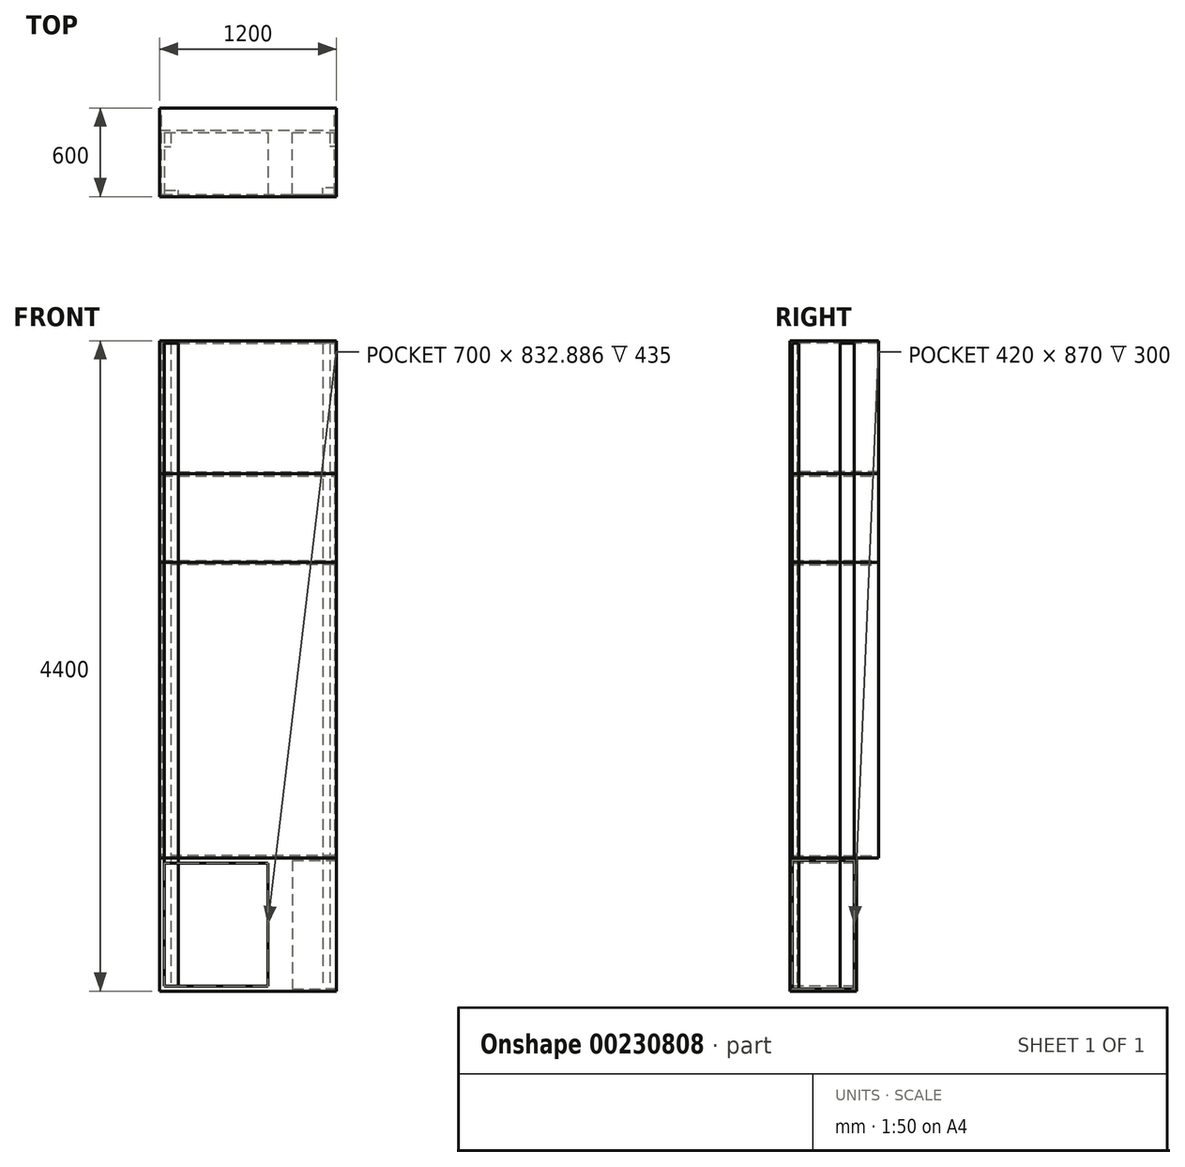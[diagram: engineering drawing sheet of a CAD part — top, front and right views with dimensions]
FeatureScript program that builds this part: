
annotation { "Feature Type Name" : "Feature", "Feature Type Description" : "" }
export const myFeature = defineFeature(function(context is Context, id is Id, definition is map)
    precondition{}
    {
        {
            var Q0;
            Q0=qCreatedBy(makeId("Top.planeOp"),FACE);
            var sketch = newSketch(context, id + "F0", { "sketchPlane" : qUnion([Q0])});
            skLineSegment(sketch, "E0.bottom", {"start": v(0, 0) * mm, "end": v(1200, 0) * mm});
            skLineSegment(sketch, "E0.top", {"start": v(0, -450) * mm, "end": v(1200, -450) * mm});
            skLineSegment(sketch, "E0.left", {"start": v(0, 0) * mm, "end": v(0, -450) * mm});
            skLineSegment(sketch, "E0.right", {"start": v(1200, 0) * mm, "end": v(1200, -450) * mm});
            skSolve(sketch);
        }
        {
            var Q0;
            Q0=makeQuery(id+"F0.imprint","IMPRINT",FACE,{"disambiguationData":[TD([[makeQuery(id+"F0.imprint","IMPRINT",EDGE,{"derivedFrom":sQuery(id+"F0.wireOp",EDGE,"E0.bottom")}),-1.0]])]});
            extrude(context, id + "F1", {"entities" : qUnion([Q0]), "oppositeDirection" : true, "depth" : 900 * mm});
        }
        {
            var Q0;
            Q0=makeQuery(id+"F1.opExtrude","CAP_FACE",FACE,{"disambiguationData":[OSD([sQuery(id+"F0.wireOp",EDGE,"E0.bottom"),sQuery(id+"F0.wireOp",EDGE,"E0.top"),sQuery(id+"F0.wireOp",EDGE,"E0.left"),sQuery(id+"F0.wireOp",EDGE,"E0.right")])],"isStart":true});
            var sketch = newSketch(context, id + "F2", { "sketchPlane" : qUnion([Q0])});
            skLineSegment(sketch, "E1.bottom", {"start": v(0, -450) * mm, "end": v(1200, -450) * mm});
            skLineSegment(sketch, "E1.top", {"start": v(0, 150) * mm, "end": v(1200, 150) * mm});
            skLineSegment(sketch, "E1.left", {"start": v(0, -450) * mm, "end": v(0, 150) * mm});
            skLineSegment(sketch, "E1.right", {"start": v(1200, -450) * mm, "end": v(1200, 150) * mm});
            skSolve(sketch);
        }
        {
            var Q0;
            Q0 = qSketchRegion(id + "F2", true);
            extrude(context, id + "F3", {"entities" : qUnion([Q0]), "depth" : 2000 * mm});
        }
        {
            var Q0;
            Q0=makeQuery(id+"F3.opExtrude","CAP_FACE",FACE,{"disambiguationData":[OSD([sQuery(id+"F2.wireOp",EDGE,"E1.bottom"),sQuery(id+"F2.wireOp",EDGE,"E1.top"),sQuery(id+"F2.wireOp",EDGE,"E1.left"),sQuery(id+"F2.wireOp",EDGE,"E1.right")])],"isStart":false});
            var sketch = newSketch(context, id + "F4", { "sketchPlane" : qUnion([Q0])});
            skLineSegment(sketch, "E2.bottom", {"start": v(1200, -450) * mm, "end": v(0, -450) * mm});
            skLineSegment(sketch, "E2.top", {"start": v(1200, 150) * mm, "end": v(0, 150) * mm});
            skLineSegment(sketch, "E2.left", {"start": v(1200, -450) * mm, "end": v(1200, 150) * mm});
            skLineSegment(sketch, "E2.right", {"start": v(0, -450) * mm, "end": v(0, 150) * mm});
            skSolve(sketch);
        }
        {
            var Q0;
            Q0 = qSketchRegion(id + "F4", true);
            extrude(context, id + "F5", {"entities" : qUnion([Q0]), "depth" : 600 * mm});
        }
        {
            var Q0;
            Q0=makeQuery(id+"F5.opExtrude","CAP_FACE",FACE,{"disambiguationData":[OSD([sQuery(id+"F4.wireOp",EDGE,"E2.bottom"),sQuery(id+"F4.wireOp",EDGE,"E2.top"),sQuery(id+"F4.wireOp",EDGE,"E2.left"),sQuery(id+"F4.wireOp",EDGE,"E2.right")])],"isStart":false});
            var sketch = newSketch(context, id + "F6", { "sketchPlane" : qUnion([Q0])});
            skLineSegment(sketch, "E3.bottom", {"start": v(1200, -450) * mm, "end": v(0, -450) * mm});
            skLineSegment(sketch, "E3.top", {"start": v(1200, 150) * mm, "end": v(0, 150) * mm});
            skLineSegment(sketch, "E3.left", {"start": v(1200, -450) * mm, "end": v(1200, 150) * mm});
            skLineSegment(sketch, "E3.right", {"start": v(0, -450) * mm, "end": v(0, 150) * mm});
            skSolve(sketch);
        }
        {
            var Q0;
            Q0=makeQuery(id+"F6.imprint","IMPRINT",FACE,{"disambiguationData":[TD([[makeQuery(id+"F6.imprint","IMPRINT",EDGE,{"derivedFrom":sQuery(id+"F6.wireOp",EDGE,"E3.bottom")}),1.0]])]});
            extrude(context, id + "F7", {"entities" : qUnion([Q0]), "depth" : 900 * mm});
        }
        {
            var Q0;
            Q0=makeQuery(id+"F1.opExtrude","SWEPT_FACE",FACE,{"disambiguationData":[OSD([sQuery(id+"F0.wireOp",EDGE,"E0.right")])]});
            var sketch = newSketch(context, id + "F8", { "sketchPlane" : qUnion([Q0])});
            skLineSegment(sketch, "E4.bottom", {"start": v(-435, -15) * mm, "end": v(-15, -15) * mm});
            skLineSegment(sketch, "E4.top", {"start": v(-435, -885) * mm, "end": v(-15, -885) * mm});
            skLineSegment(sketch, "E4.left", {"start": v(-435, -15) * mm, "end": v(-435, -885) * mm});
            skLineSegment(sketch, "E4.right", {"start": v(-15, -15) * mm, "end": v(-15, -885) * mm});
            skLineSegment(sketch, "E5.bottom", {"start": v(-435, -15) * mm, "end": v(-450, -15) * mm, "construction": true});
            skLineSegment(sketch, "E5.top", {"start": v(-435, -15) * mm, "end": v(-450, -15) * mm, "construction": true});
            skLineSegment(sketch, "E5.left", {"start": v(-435, -15) * mm, "end": v(-435, -15) * mm});
            skLineSegment(sketch, "E5.right", {"start": v(-450, -15) * mm, "end": v(-450, -15) * mm});
            skLineSegment(sketch, "E6.top", {"start": v(-435, 0) * mm, "end": v(-435, 0) * mm});
            skLineSegment(sketch, "E6.left", {"start": v(-435, -15) * mm, "end": v(-435, 0) * mm, "construction": true});
            skLineSegment(sketch, "E6.right", {"start": v(-435, -15) * mm, "end": v(-435, 0) * mm, "construction": true});
            skLineSegment(sketch, "E7.bottom", {"start": v(-15, -885) * mm, "end": v(0, -885) * mm, "construction": true});
            skLineSegment(sketch, "E7.top", {"start": v(-15, -885) * mm, "end": v(0, -885) * mm, "construction": true});
            skLineSegment(sketch, "E7.left", {"start": v(-15, -885) * mm, "end": v(-15, -885) * mm});
            skLineSegment(sketch, "E7.right", {"start": v(0, -885) * mm, "end": v(0, -885) * mm});
            skLineSegment(sketch, "E8.top", {"start": v(-15, -900) * mm, "end": v(-15, -900) * mm});
            skLineSegment(sketch, "E8.left", {"start": v(-15, -885) * mm, "end": v(-15, -900) * mm, "construction": true});
            skLineSegment(sketch, "E8.right", {"start": v(-15, -885) * mm, "end": v(-15, -900) * mm, "construction": true});
            skSolve(sketch);
        }
        {
            var Q0;
            Q0=makeQuery(id+"F8.imprint","IMPRINT",FACE,{"disambiguationData":[TD([[makeQuery(id+"F8.imprint","IMPRINT",EDGE,{"derivedFrom":sQuery(id+"F8.wireOp",EDGE,"E4.bottom")}),-1.0]])]});
            extrude(context, id + "F9", {"entities" : qUnion([Q0]), "operationType" : NewBodyOperationType.REMOVE, "oppositeDirection" : true, "depth" : 300 * mm});
        }
        {
            var Q0;
            Q0=makeQuery(id+"F1.opExtrude","SWEPT_FACE",FACE,{"disambiguationData":[OSD([sQuery(id+"F0.wireOp",EDGE,"E0.top")])]});
            var sketch = newSketch(context, id + "F10", { "sketchPlane" : qUnion([Q0])});
            skLineSegment(sketch, "E9.bottom", {"start": v(33.56, -33.56) * mm, "end": v(733.56, -33.56) * mm});
            skLineSegment(sketch, "E9.top", {"start": v(33.56, -866.44) * mm, "end": v(733.56, -866.44) * mm});
            skLineSegment(sketch, "E9.left", {"start": v(33.56, -33.56) * mm, "end": v(33.56, -866.44) * mm});
            skLineSegment(sketch, "E9.right", {"start": v(733.56, -33.56) * mm, "end": v(733.56, -866.44) * mm});
            skLineSegment(sketch, "E10.bottom", {"start": v(33.56, -33.56) * mm, "end": v(33.56, -33.56) * mm});
            skLineSegment(sketch, "E10.top", {"start": v(33.56, 0) * mm, "end": v(33.56, 0) * mm});
            skLineSegment(sketch, "E10.left", {"start": v(33.56, -33.56) * mm, "end": v(33.56, 0) * mm, "construction": true});
            skLineSegment(sketch, "E10.right", {"start": v(33.56, -33.56) * mm, "end": v(33.56, 0) * mm, "construction": true});
            skLineSegment(sketch, "E11.bottom", {"start": v(33.56, -33.56) * mm, "end": v(0, -33.56) * mm, "construction": true});
            skLineSegment(sketch, "E11.top", {"start": v(33.56, -33.56) * mm, "end": v(0, -33.56) * mm, "construction": true});
            skLineSegment(sketch, "E11.right", {"start": v(0, -33.56) * mm, "end": v(0, -33.56) * mm});
            skLineSegment(sketch, "E12.bottom", {"start": v(733.56, -866.44) * mm, "end": v(733.56, -866.44) * mm});
            skLineSegment(sketch, "E12.top", {"start": v(733.56, -900) * mm, "end": v(733.56, -900) * mm});
            skLineSegment(sketch, "E12.left", {"start": v(733.56, -866.44) * mm, "end": v(733.56, -900) * mm, "construction": true});
            skLineSegment(sketch, "E12.right", {"start": v(733.56, -866.44) * mm, "end": v(733.56, -900) * mm, "construction": true});
            skSolve(sketch);
        }
        {
            var Q0;
            Q0=makeQuery(id+"F10.imprint","IMPRINT",FACE,{"disambiguationData":[TD([[makeQuery(id+"F10.imprint","IMPRINT",EDGE,{"derivedFrom":sQuery(id+"F10.wireOp",EDGE,"E9.bottom")}),-1.0]])]});
            extrude(context, id + "F11", {"entities" : qUnion([Q0]), "operationType" : NewBodyOperationType.REMOVE, "oppositeDirection" : true, "depth" : 435 * mm});
        }
        {
            var Q0;
            Q0=makeQuery(id+"F3.opExtrude","SWEPT_FACE",FACE,{"disambiguationData":[OSD([sQuery(id+"F2.wireOp",EDGE,"E1.top")])]});
            var sketch = newSketch(context, id + "F12", { "sketchPlane" : qUnion([Q0])});
            skLineSegment(sketch, "E13.bottom", {"start": v(-1185, 1985) * mm, "end": v(-15, 1985) * mm});
            skLineSegment(sketch, "E13.top", {"start": v(-1185, 15) * mm, "end": v(-15, 15) * mm});
            skLineSegment(sketch, "E13.left", {"start": v(-1185, 1985) * mm, "end": v(-1185, 15) * mm});
            skLineSegment(sketch, "E13.right", {"start": v(-15, 1985) * mm, "end": v(-15, 15) * mm});
            skLineSegment(sketch, "E14.bottom", {"start": v(-1185, 1985) * mm, "end": v(-1185, 1985) * mm});
            skLineSegment(sketch, "E14.top", {"start": v(-1185, 2000) * mm, "end": v(-1185, 2000) * mm});
            skLineSegment(sketch, "E14.left", {"start": v(-1185, 1985) * mm, "end": v(-1185, 2000) * mm, "construction": true});
            skLineSegment(sketch, "E14.right", {"start": v(-1185, 1985) * mm, "end": v(-1185, 2000) * mm, "construction": true});
            skLineSegment(sketch, "E15.bottom", {"start": v(-1185, 1985) * mm, "end": v(-1200, 1985) * mm, "construction": true});
            skLineSegment(sketch, "E15.top", {"start": v(-1185, 1985) * mm, "end": v(-1200, 1985) * mm, "construction": true});
            skLineSegment(sketch, "E15.right", {"start": v(-1200, 1985) * mm, "end": v(-1200, 1985) * mm});
            skLineSegment(sketch, "E16.bottom", {"start": v(-15, 15) * mm, "end": v(0, 15) * mm, "construction": true});
            skLineSegment(sketch, "E16.top", {"start": v(-15, 15) * mm, "end": v(0, 15) * mm, "construction": true});
            skLineSegment(sketch, "E16.left", {"start": v(-15, 15) * mm, "end": v(-15, 15) * mm});
            skLineSegment(sketch, "E16.right", {"start": v(0, 15) * mm, "end": v(0, 15) * mm});
            skLineSegment(sketch, "E17.top", {"start": v(-15, 0) * mm, "end": v(-15, 0) * mm});
            skLineSegment(sketch, "E17.left", {"start": v(-15, 15) * mm, "end": v(-15, 0) * mm, "construction": true});
            skLineSegment(sketch, "E17.right", {"start": v(-15, 15) * mm, "end": v(-15, 0) * mm, "construction": true});
            skSolve(sketch);
        }
        {
            var Q0;
            Q0 = qSketchRegion(id + "F12", true);
            extrude(context, id + "F13", {"entities" : qUnion([Q0]), "operationType" : NewBodyOperationType.REMOVE, "oppositeDirection" : true, "depth" : 585 * mm});
        }
        {
            var Q0;
            Q0=makeQuery(id+"F5.opExtrude","SWEPT_FACE",FACE,{"disambiguationData":[OSD([sQuery(id+"F4.wireOp",EDGE,"E2.top")])]});
            var sketch = newSketch(context, id + "F14", { "sketchPlane" : qUnion([Q0])});
            skLineSegment(sketch, "E18.bottom", {"start": v(-15, 2585) * mm, "end": v(-1185, 2585) * mm});
            skLineSegment(sketch, "E18.top", {"start": v(-15, 2015) * mm, "end": v(-1185, 2015) * mm});
            skLineSegment(sketch, "E18.left", {"start": v(-15, 2585) * mm, "end": v(-15, 2015) * mm});
            skLineSegment(sketch, "E18.right", {"start": v(-1185, 2585) * mm, "end": v(-1185, 2015) * mm});
            skLineSegment(sketch, "E19.bottom", {"start": v(-1185, 2585) * mm, "end": v(-1185, 2585) * mm});
            skLineSegment(sketch, "E19.top", {"start": v(-1185, 2600) * mm, "end": v(-1185, 2600) * mm});
            skLineSegment(sketch, "E19.left", {"start": v(-1185, 2585) * mm, "end": v(-1185, 2600) * mm, "construction": true});
            skLineSegment(sketch, "E19.right", {"start": v(-1185, 2585) * mm, "end": v(-1185, 2600) * mm, "construction": true});
            skLineSegment(sketch, "E20.bottom", {"start": v(-1185, 2585) * mm, "end": v(-1200, 2585) * mm, "construction": true});
            skLineSegment(sketch, "E20.top", {"start": v(-1185, 2585) * mm, "end": v(-1200, 2585) * mm, "construction": true});
            skLineSegment(sketch, "E20.right", {"start": v(-1200, 2585) * mm, "end": v(-1200, 2585) * mm});
            skLineSegment(sketch, "E21.bottom", {"start": v(-15, 2015) * mm, "end": v(0, 2015) * mm, "construction": true});
            skLineSegment(sketch, "E21.top", {"start": v(-15, 2015) * mm, "end": v(0, 2015) * mm, "construction": true});
            skLineSegment(sketch, "E21.left", {"start": v(-15, 2015) * mm, "end": v(-15, 2015) * mm});
            skLineSegment(sketch, "E21.right", {"start": v(0, 2015) * mm, "end": v(0, 2015) * mm});
            skLineSegment(sketch, "E22.top", {"start": v(-15, 2000) * mm, "end": v(-15, 2000) * mm});
            skLineSegment(sketch, "E22.left", {"start": v(-15, 2015) * mm, "end": v(-15, 2000) * mm, "construction": true});
            skLineSegment(sketch, "E22.right", {"start": v(-15, 2015) * mm, "end": v(-15, 2000) * mm, "construction": true});
            skSolve(sketch);
        }
        {
            var Q0;
            Q0=makeQuery(id+"F14.imprint","IMPRINT",FACE,{"disambiguationData":[TD([[makeQuery(id+"F14.imprint","IMPRINT",EDGE,{"derivedFrom":sQuery(id+"F14.wireOp",EDGE,"E18.bottom")}),1.0]])]});
            extrude(context, id + "F15", {"entities" : qUnion([Q0]), "operationType" : NewBodyOperationType.REMOVE, "oppositeDirection" : true, "depth" : 585 * mm});
        }
        {
            var Q0;
            Q0=makeQuery(id+"F7.opExtrude","SWEPT_FACE",FACE,{"disambiguationData":[OSD([sQuery(id+"F6.wireOp",EDGE,"E3.top")])]});
            var Q1;
            Q1=makeQuery(id+"F7.opExtrude","SWEPT_BODY",BODY,{"disambiguationData":[OSD([sQuery(id+"F6.wireOp",EDGE,"E3.bottom"),sQuery(id+"F6.wireOp",EDGE,"E3.top"),sQuery(id+"F6.wireOp",EDGE,"E3.left"),sQuery(id+"F6.wireOp",EDGE,"E3.right")])]});
            shell(context, id + "F16", {"entities" : qUnion([Q0]), "parts" : qUnion([Q1]), "thickness" : 15 * mm});
        }
        {
            var Q0;
            Q0=makeQuery(id+"F9.boolean.opBoolean","COPY",FACE,{"derivedFrom":makeQuery(id+"F9.opExtrude","SWEPT_FACE",FACE,{"disambiguationData":[OSD([sQuery(id+"F8.wireOp",EDGE,"E4.top")])]})});
            var sketch = newSketch(context, id + "F17", { "sketchPlane" : qUnion([Q0])});
            skLineSegment(sketch, "E23.bottom", {"start": v(1200, -435) * mm, "end": v(1105, -435) * mm});
            skLineSegment(sketch, "E23.top", {"start": v(1200, -390) * mm, "end": v(1105, -390) * mm});
            skLineSegment(sketch, "E23.left", {"start": v(1200, -435) * mm, "end": v(1200, -390) * mm});
            skLineSegment(sketch, "E23.right", {"start": v(1105, -435) * mm, "end": v(1105, -390) * mm});
            skSolve(sketch);
        }
        {
            var Q0;
            Q0=makeQuery(id+"F17.imprint","IMPRINT",FACE,{"disambiguationData":[TD([[makeQuery(id+"F17.imprint","IMPRINT",EDGE,{"derivedFrom":sQuery(id+"F17.wireOp",EDGE,"E23.bottom")}),1.0]])]});
            var Q1;
            {var subQ0=sQuery(id+"F6.wireOp",EDGE,"E3.right");var subQ1=sQuery(id+"F6.wireOp",EDGE,"E3.left");var subQ2=sQuery(id+"F6.wireOp",EDGE,"E3.top");var subQ3=sQuery(id+"F6.wireOp",EDGE,"E3.bottom");Q1=makeQuery(id+"F16.opShell","OFFSET_FACE",FACE,{"disambiguationData":[OSD([subQ3,subQ2,subQ1,subQ0]),TDD([makeQuery(id+"F7.opExtrude","CAP_FACE",FACE,{"disambiguationData":[OSD([subQ3,subQ2,subQ1,subQ0])],"isStart":false})])]});}
            extrude(context, id + "F18", {"entities" : qUnion([Q0]), "endBound" : BoundingType.UP_TO_SURFACE, "endBoundEntityFace" : qUnion([Q1]), "depth" : 25 * mm});
        }
        {
            var Q0;
            Q0=makeQuery(id+"F11.boolean.opBoolean","COPY",FACE,{"derivedFrom":makeQuery(id+"F11.opExtrude","SWEPT_FACE",FACE,{"disambiguationData":[OSD([sQuery(id+"F10.wireOp",EDGE,"E9.top")])]})});
            var sketch = newSketch(context, id + "F19", { "sketchPlane" : qUnion([Q0])});
            skLineSegment(sketch, "E24.bottom", {"start": v(33.56, -450) * mm, "end": v(128.56, -450) * mm});
            skLineSegment(sketch, "E24.top", {"start": v(33.56, -405) * mm, "end": v(128.56, -405) * mm});
            skLineSegment(sketch, "E24.left", {"start": v(33.56, -450) * mm, "end": v(33.56, -405) * mm});
            skLineSegment(sketch, "E24.right", {"start": v(128.56, -450) * mm, "end": v(128.56, -405) * mm});
            skSolve(sketch);
        }
        {
            var Q0;
            Q0=makeQuery(id+"F19.imprint","IMPRINT",FACE,{"disambiguationData":[TD([[makeQuery(id+"F19.imprint","IMPRINT",EDGE,{"derivedFrom":sQuery(id+"F19.wireOp",EDGE,"E24.bottom")}),1.0]])]});
            var Q1;
            {var subQ0=sQuery(id+"F6.wireOp",EDGE,"E3.right");var subQ1=sQuery(id+"F6.wireOp",EDGE,"E3.left");var subQ2=sQuery(id+"F6.wireOp",EDGE,"E3.top");var subQ3=sQuery(id+"F6.wireOp",EDGE,"E3.bottom");Q1=makeQuery(id+"F16.opShell","OFFSET_FACE",FACE,{"disambiguationData":[OSD([subQ3,subQ2,subQ1,subQ0]),TDD([makeQuery(id+"F7.opExtrude","CAP_FACE",FACE,{"disambiguationData":[OSD([subQ3,subQ2,subQ1,subQ0])],"isStart":false})])]});}
            extrude(context, id + "F20", {"entities" : qUnion([Q0]), "endBound" : BoundingType.UP_TO_SURFACE, "endBoundEntityFace" : qUnion([Q1]), "depth" : 25 * mm});
        }
        {
            var Q0;
            Q0=makeQuery(id+"F11.boolean.opBoolean","COPY",FACE,{"derivedFrom":makeQuery(id+"F11.opExtrude","SWEPT_FACE",FACE,{"disambiguationData":[OSD([sQuery(id+"F10.wireOp",EDGE,"E9.top")])]})});
            var sketch = newSketch(context, id + "F21", { "sketchPlane" : qUnion([Q0])});
            skLineSegment(sketch, "E25.bottom", {"start": v(33.56, -15) * mm, "end": v(78.56, -15) * mm});
            skLineSegment(sketch, "E25.top", {"start": v(33.56, -110) * mm, "end": v(78.56, -110) * mm});
            skLineSegment(sketch, "E25.left", {"start": v(33.56, -15) * mm, "end": v(33.56, -110) * mm});
            skLineSegment(sketch, "E25.right", {"start": v(78.56, -15) * mm, "end": v(78.56, -110) * mm});
            skSolve(sketch);
        }
        {
            var Q0;
            Q0=makeQuery(id+"F21.imprint","IMPRINT",FACE,{"disambiguationData":[TD([[makeQuery(id+"F21.imprint","IMPRINT",EDGE,{"derivedFrom":sQuery(id+"F21.wireOp",EDGE,"E25.bottom")}),-1.0]])]});
            var Q1;
            {var subQ0=sQuery(id+"F6.wireOp",EDGE,"E3.right");var subQ1=sQuery(id+"F6.wireOp",EDGE,"E3.left");var subQ2=sQuery(id+"F6.wireOp",EDGE,"E3.top");var subQ3=sQuery(id+"F6.wireOp",EDGE,"E3.bottom");Q1=makeQuery(id+"F16.opShell","OFFSET_FACE",FACE,{"disambiguationData":[OSD([subQ3,subQ2,subQ1,subQ0]),TDD([makeQuery(id+"F7.opExtrude","CAP_FACE",FACE,{"disambiguationData":[OSD([subQ3,subQ2,subQ1,subQ0])],"isStart":false})])]});}
            extrude(context, id + "F22", {"entities" : qUnion([Q0]), "endBound" : BoundingType.UP_TO_SURFACE, "endBoundEntityFace" : qUnion([Q1]), "depth" : 25 * mm});
        }
        {
            var Q0;
            Q0=makeQuery(id+"F9.boolean.opBoolean","COPY",FACE,{"derivedFrom":makeQuery(id+"F9.opExtrude","SWEPT_FACE",FACE,{"disambiguationData":[OSD([sQuery(id+"F8.wireOp",EDGE,"E4.top")])]})});
            var sketch = newSketch(context, id + "F23", { "sketchPlane" : qUnion([Q0])});
            skLineSegment(sketch, "E26.bottom", {"start": v(1200, -15) * mm, "end": v(1155, -15) * mm});
            skLineSegment(sketch, "E26.top", {"start": v(1200, -110) * mm, "end": v(1155, -110) * mm});
            skLineSegment(sketch, "E26.left", {"start": v(1200, -15) * mm, "end": v(1200, -110) * mm});
            skLineSegment(sketch, "E26.right", {"start": v(1155, -15) * mm, "end": v(1155, -110) * mm});
            skSolve(sketch);
        }
        {
            var Q0;
            Q0=makeQuery(id+"F23.imprint","IMPRINT",FACE,{"disambiguationData":[TD([[makeQuery(id+"F23.imprint","IMPRINT",EDGE,{"derivedFrom":sQuery(id+"F23.wireOp",EDGE,"E26.bottom")}),-1.0]])]});
            var Q1;
            {var subQ0=sQuery(id+"F6.wireOp",EDGE,"E3.right");var subQ1=sQuery(id+"F6.wireOp",EDGE,"E3.left");var subQ2=sQuery(id+"F6.wireOp",EDGE,"E3.top");var subQ3=sQuery(id+"F6.wireOp",EDGE,"E3.bottom");Q1=makeQuery(id+"F16.opShell","OFFSET_FACE",FACE,{"disambiguationData":[OSD([subQ3,subQ2,subQ1,subQ0]),TDD([makeQuery(id+"F7.opExtrude","CAP_FACE",FACE,{"disambiguationData":[OSD([subQ3,subQ2,subQ1,subQ0])],"isStart":false})])]});}
            extrude(context, id + "F24", {"entities" : qUnion([Q0]), "endBound" : BoundingType.UP_TO_SURFACE, "endBoundEntityFace" : qUnion([Q1]), "depth" : 25 * mm});
        }
    });
